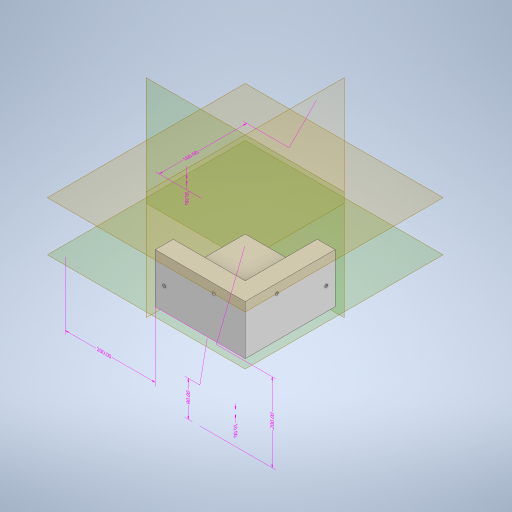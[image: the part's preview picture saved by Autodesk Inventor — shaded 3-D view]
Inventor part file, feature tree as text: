
AUTODESK INVENTOR PART (.ipt)
format: ipt  version: 2023 (Build 270158000, 158)  size: 436,736 bytes
history: native  units: mm
features: sketch x9, other x8, extrude x5, hole x4, plane x4, split x4
ambient origin geometry x8: Origin, YZ Plane, XZ Plane, XY Plane, X Axis, Y Axis, Z Axis, Center Point
bodies: Body1 (feature_tree)
feature tree (34):
  other  "Sólido1"
  other  "Anotaciones"
  extrude  "Extrusión1"  Depth=200.0mm
  hole  "Agujero1"  [1 undecoded]
  extrude  "Extrusión2"  Depth=15.0mm
  extrude  "Extrusión3"  Depth=80.0mm TaperAngle=0.0deg
  extrude  "Extrusión4"  Depth=200.0mm
  extrude  "Extrusión5"  Depth=20.0mm
  hole  "Agujero2"  [1 undecoded]
  plane  "Plano de trabajo1"
  split  "Dividir1"
  plane  "Plano de trabajo2"
  plane  "Plano de trabajo3"
  plane  "Plano de trabajo4"
  hole  "Agujero3"  [1 undecoded]
  hole  "Agujero4"  [1 undecoded]
  split  "Dividir2"
  split  "Dividir3"
  split  "Dividir4"
  sketch  "Boceto2"  dims[d7=15.0mm d8=200.0mm]
  sketch  "Boceto3"  dims[d9=10.0mm d10=0.0mm]
  sketch  "Boceto4"  dims[d11=3.5mm d12=1.75mm d13=1.75mm d14=1.75mm d15=1.75mm d16=10.0mm d17=10.0mm d19=40.0mm]
  sketch  "Boceto5"  dims[d20=3.5mm d21=6.0mm d22=4.0mm d23=2.0mm d24=90.0deg d25=8.0mm d26=20.594885mm d27=15.0mm]
  sketch  "Boceto6"  dims[d28=20.0mm d29=80.0mm d30=0.0mm]
  sketch  "Boceto7"  dims[d31=57.0mm d32=200.0mm]
  sketch  "Boceto8"  dims[d33=110.0mm d34=0.0mm d36=20.0mm]
  sketch  "Boceto9"  dims[d37=20.0mm d38=20.0mm]
  sketch  "Boceto10"  dims[d39=90.0mm d40=0.0mm d43=30.0mm d44=0.0mm d45=3.5mm d46=1.75mm d47=1.75mm d48=1.75mm d49=1.75mm d50=10.0mm d51=10.0mm d52=15.0mm d53=10.0mm d54=10.0mm d55=15.0mm d56=3.5mm d57=6.0mm d58=4.0mm d59=2.0mm d60=90.0deg d61=8.0mm d62=20.594885mm d63=10.0mm d65=10.0mm d75=200.0mm d76=10.0mm d77=20.0mm d81=40.0mm d88=90.0deg d89=10.0mm d90=30.0mm d91=5.0mm d92=5.0mm d93=5.0mm d94=5.0mm d95=30.0mm d96=5.0mm d97=5.0mm d98=3.5mm d99=5.0mm d100=5.0mm d101=5.0mm d102=5.0mm d103=5.0mm d104=20.0mm d105=3.5mm d106=6.0mm d107=4.0mm d108=2.0mm d109=90.0deg d110=8.0mm d111=20.594885mm d112=10.0mm d113=30.0mm d114=5.0mm d115=5.0mm d116=5.0mm d117=5.0mm d118=5.0mm d119=5.0mm d120=3.5mm d121=5.0mm d122=5.0mm d123=5.0mm d124=5.0mm d125=5.0mm d126=30.0mm d127=30.0mm d128=3.5mm d129=6.0mm d130=4.0mm d131=2.0mm d132=90.0deg d133=8.0mm d134=20.594885mm d66=5.760865mm d67=7.72461mm d68=200.0mm d69=3.008686mm d70=2.422102mm d71=10.0mm d72=3.500509mm d73=2.402572mm d74=90.0mm d78=3.13122mm d79=6.269346mm d80=200.0mm d82=8.450127mm d83=0.968417mm d84=20.0mm d85=4.759975mm d86=4.646891mm d87=160.0mm]
  other  "Cota lineal 1"
  other  "Cota lineal 2"
  other  "Cota lineal 3"
  other  "Cota lineal 4"
  other  "Cota lineal 5"
  other  "Cota lineal 6"
note: 4 required parameter values undecoded (feature->parameter linkage not recoverable at this tier; creation-order binding heuristic only, values carry confidence <= 0.55)
